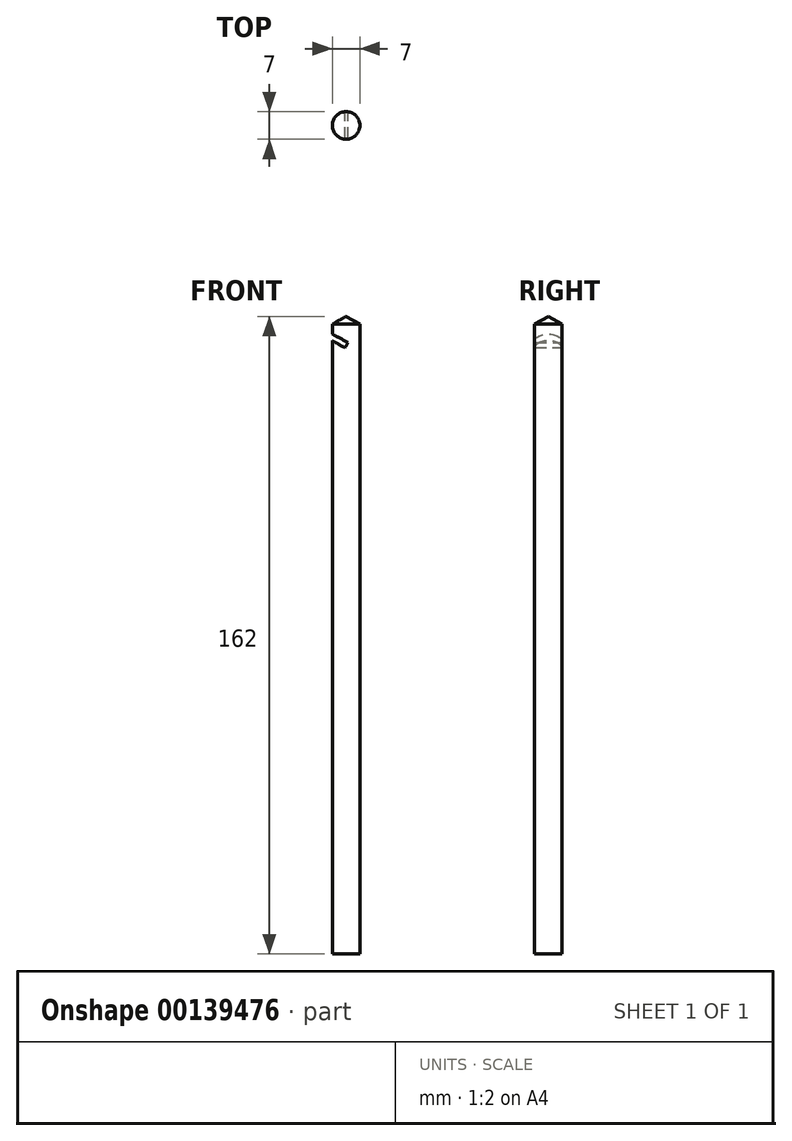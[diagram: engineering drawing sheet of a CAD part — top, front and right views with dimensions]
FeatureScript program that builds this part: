
annotation { "Feature Type Name" : "Feature", "Feature Type Description" : "" }
export const myFeature = defineFeature(function(context is Context, id is Id, definition is map)
    precondition{}
    {
        {
            var Q0;
            Q0=qCreatedBy(makeId("Front.planeOp"),FACE);
            var sketch = newSketch(context, id + "F0", { "sketchPlane" : qUnion([Q0])});
            skLineSegment(sketch, "E0", {"start": v(0, 0) * mm, "end": v(-9, 0) * mm});
            skLineSegment(sketch, "E1", {"start": v(-9, 0) * mm, "end": v(-9, 40) * mm});
            skLineSegment(sketch, "E2", {"start": v(0, 166) * mm, "end": v(0, 0) * mm});
            skLineSegment(sketch, "E3", {"start": v(-9, 40) * mm, "end": v(-8, 40) * mm});
            skLineSegment(sketch, "E4", {"start": v(-8, 40) * mm, "end": v(-8, 80) * mm});
            skLineSegment(sketch, "E5", {"start": v(-8, 80) * mm, "end": v(-6, 80) * mm});
            skLineSegment(sketch, "E6", {"start": v(-6, 80) * mm, "end": v(-6, 160) * mm});
            skLineSegment(sketch, "E7", {"start": v(0, 166) * mm, "end": v(0, 166) * mm});
            skPoint(sketch, "E8.visualSharp", {"position": v(-6, 166) * mm});
            skArc(sketch, "E8.filletArc", {"start": v(0, 166) * mm, "mid": v(-4.24, 164.24) * mm, "end": v(-6, 160) * mm});
            skLineSegment(sketch, "E9", {"start": v(0, 0) * mm, "end": v(-3.5, 0) * mm});
            skLineSegment(sketch, "E10", {"start": v(0, 153.17) * mm, "end": v(0, 0) * mm});
            skLineSegment(sketch, "E11", {"start": v(-3.5, 0) * mm, "end": v(-3.5, 160) * mm});
            skLineSegment(sketch, "E12", {"start": v(-3.5, 160) * mm, "end": v(0, 162) * mm});
            skLineSegment(sketch, "E13", {"start": v(0, 162) * mm, "end": v(0, 0) * mm});
            skSolve(sketch);
        }
        {
            var Q0;
            Q0=makeQuery(id+"F0.imprint","IMPRINT",FACE,{"disambiguationData":[TD([[makeQuery(id+"F0.imprint","IMPRINT",EDGE,{"derivedFrom":sQuery(id+"F0.wireOp",EDGE,"E0")}),-1.0]])]});
            var Q1;
            Q1=sQuery(id+"F0.wireOp",EDGE,"E2");
            revolve(context, id + "F1", {"entities" : qUnion([Q0]), "axis" : qUnion([Q1]), "revolveType" : RevolveType.FULL});
        }
        {
            var Q0;
            Q0=qCreatedBy(makeId("Front.planeOp"),FACE);
            var sketch = newSketch(context, id + "F2", { "sketchPlane" : qUnion([Q0])});
            skLineSegment(sketch, "E14", {"start": v(-11.03, 40.47) * mm, "end": v(-8.03, 40.47) * mm});
            skLineSegment(sketch, "E15", {"start": v(-8.03, 40.47) * mm, "end": v(-8.03, 29.47) * mm});
            skLineSegment(sketch, "E16", {"start": v(-8.03, 29.47) * mm, "end": v(-11.03, 29.47) * mm});
            skLineSegment(sketch, "E17", {"start": v(-11.03, 29.47) * mm, "end": v(-11.03, 40.47) * mm});
            skSolve(sketch);
        }
        {
            var Q0;
            Q0=qSketchRegion(id+"F2",true);
            extrude(context, id + "F3", {"entities" : qUnion([Q0]), "operationType" : NewBodyOperationType.REMOVE, "endBound" : BoundingType.THROUGH_ALL, "oppositeDirection" : true, "depth" : 15 * mm, "hasSecondDirection" : true, "secondDirectionBound" : SecondDirectionBoundingType.THROUGH_ALL, "secondDirectionOppositeDirection" : false, "secondDirectionDepth" : 25 * mm});
        }
        {
            var Q0;
            Q0=qCreatedBy(makeId("Front.planeOp"),FACE);
            var sketch = newSketch(context, id + "F4", { "sketchPlane" : qUnion([Q0])});
            skLineSegment(sketch, "E18", {"start": v(8.02, 40.84) * mm, "end": v(11.02, 40.84) * mm});
            skLineSegment(sketch, "E19", {"start": v(11.02, 40.84) * mm, "end": v(11.02, 24.84) * mm});
            skLineSegment(sketch, "E20", {"start": v(11.02, 24.84) * mm, "end": v(8.02, 24.84) * mm});
            skLineSegment(sketch, "E21", {"start": v(8.02, 24.84) * mm, "end": v(8.02, 40.84) * mm});
            skSolve(sketch);
        }
        {
            var Q0;
            Q0=qSketchRegion(id+"F4",true);
            extrude(context, id + "F5", {"entities" : qUnion([Q0]), "operationType" : NewBodyOperationType.REMOVE, "endBound" : BoundingType.THROUGH_ALL, "oppositeDirection" : true, "depth" : 25 * mm, "hasSecondDirection" : true, "secondDirectionBound" : SecondDirectionBoundingType.THROUGH_ALL, "secondDirectionOppositeDirection" : false, "secondDirectionDepth" : 25 * mm});
        }
        {
            var Q0;
            Q0=qCreatedBy(makeId("Front.planeOp"),FACE);
            var sketch = newSketch(context, id + "F6", { "sketchPlane" : qUnion([Q0])});
            skLineSegment(sketch, "E22", {"start": v(-9.04, 158.8) * mm, "end": v(-0.26, 154.02) * mm});
            skLineSegment(sketch, "E23", {"start": v(-0.26, 154.02) * mm, "end": v(0.46, 155.33) * mm});
            skLineSegment(sketch, "E24", {"start": v(0.46, 155.33) * mm, "end": v(-8.32, 160.11) * mm});
            skLineSegment(sketch, "E25", {"start": v(-8.32, 160.11) * mm, "end": v(-9.04, 158.8) * mm});
            skSolve(sketch);
        }
        {
            var Q0;
            Q0=makeQuery(id+"F6.imprint","IMPRINT",FACE,{"disambiguationData":[TD([[makeQuery(id+"F6.imprint","IMPRINT",EDGE,{"derivedFrom":sQuery(id+"F6.wireOp",EDGE,"E22")}),1.0]])]});
            extrude(context, id + "F7", {"entities" : qUnion([Q0]), "operationType" : NewBodyOperationType.REMOVE, "endBound" : BoundingType.THROUGH_ALL, "depth" : 25 * mm, "hasSecondDirection" : true, "secondDirectionBound" : SecondDirectionBoundingType.THROUGH_ALL, "secondDirectionOppositeDirection" : true, "secondDirectionDepth" : 25 * mm});
        }
    });
